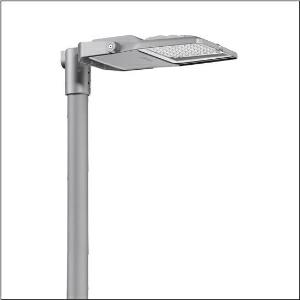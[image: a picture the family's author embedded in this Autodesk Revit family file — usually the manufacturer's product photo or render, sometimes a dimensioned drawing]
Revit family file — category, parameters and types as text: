
# Revit family: floodlight_fl_21_mini___pl43_5xa7775d2a3a_0001
name_source: partatom
category: Lighting Fixtures
units: mm (PartAtom-declared; Revit-internal decimal feet)

## family parameters
Cut with Voids When Loaded = No
Host = Face
Light Source = No
Part Type = Normal
Room Calculation Point = No
Round Connector Dimension = Use Diameter
Shared = No

## types (1)
- --- (1 x LED, 18300 lm, 142.9 W, 3000K)
    Apparent Load = 143 VA
    CIE Flux Codes = 27 78 99 100 100
    Color Rendering = 70
    Color Temperature = 3000K
    Default Elevation = 1800 mm
    Description = Floodlight FL 21 mini, floodlight, primary light control with lens, of PMMA, primary optical cover: protective disc, of toughened safety glass, transparent, light distribution: PL43, light emission: direct distribution, installation type: surface-mounted, LED, High Power LED, rated luminous flux: 18.300lm, luminous efficacy: 128lm/W, light colour: 730, colour temperature: 3000K, control: flexible luminous flux parameterisation, time-dependent luminous flux control, constant luminous flux control, overheat protection, presetting dimming logarithmic, with terminal, 6-pole, mains connection: 220..240V, AC, 50/60Hz, start of lifetime: 143W, end of service life: 151W, reduction: 63W, luminaire housing, of diecast aluminium, powder-coated, Siteco® metallic grey (DB 702S), corrosivity category C5 mid according to DIN EN ISO 12944, sealing non-destructively replaceable, please order mast flange separately, mast bracket, of steel, galvanised, powder-coated, Siteco® metallic grey (DB 702S), Smart Interface above, protection rating (complete): IP66, insulation class (complete): insulation class II (safety insulation), certification: CE, ENEC, VDE, protection symbol: D, impact resistance: IK08, permissible operating ambient temperature: -40..+40°C, permissible operating ambient temperature for outdoor applications: -40..+50°C, standard: DIN EN 12944, LABS conformity tested according to VDMA 24364:2018-05, packaging unit: 1 piece

Light Distribution: PL43
    Height = 70 mm
    Lamp = 1 x LED
    Lamp Light Flux = 18300 lm
    Lamp Power = 142.9 W
    Lamp count = 1
    Length = 485 mm
    Luminous efficacy = 128 lm/W
    Manufacturer = Siteco
    ModVariant = No
    Model = 5XA7775D2A3A
    Number of Poles = 1
    OnlyDefault = Yes
    Power Factor = 1
    Product Name = Floodlight FL 21 mini | PL43
    Product group = floodlight | pylon annexe
    ProductGroupID = 6200
    Protection Class = Protection class II
    Protection Degree = IP 66
    RLX_Detail_Level = 1
    RLX_Emergency_Light_Flux = 0 lm
    RLX_Emergency_Type = 0
    RLX_Emergency_Type_DB = No
    RlxData = <blob elided: 101033 chars, md5=ec4a055c>
    Socket = socket
    Standby Power = 0 W
    System Light Flux = 18300 lm
    System Power = 143 W
    Type Comments = factory setting: luminous flux: 100 % | dim-lin: 254 | 730 mA
    Type Image = l_1007125.jpg
    URL = http://relux.com
    VarID = @adj_093287
    Voltage = 0 V
    Weight = 0.00 kg
    Width = 337 mm

## geometry (parser evidence)
native form markers: Blend x4, Sweep x11
no freeform markers — native parametric forms only
